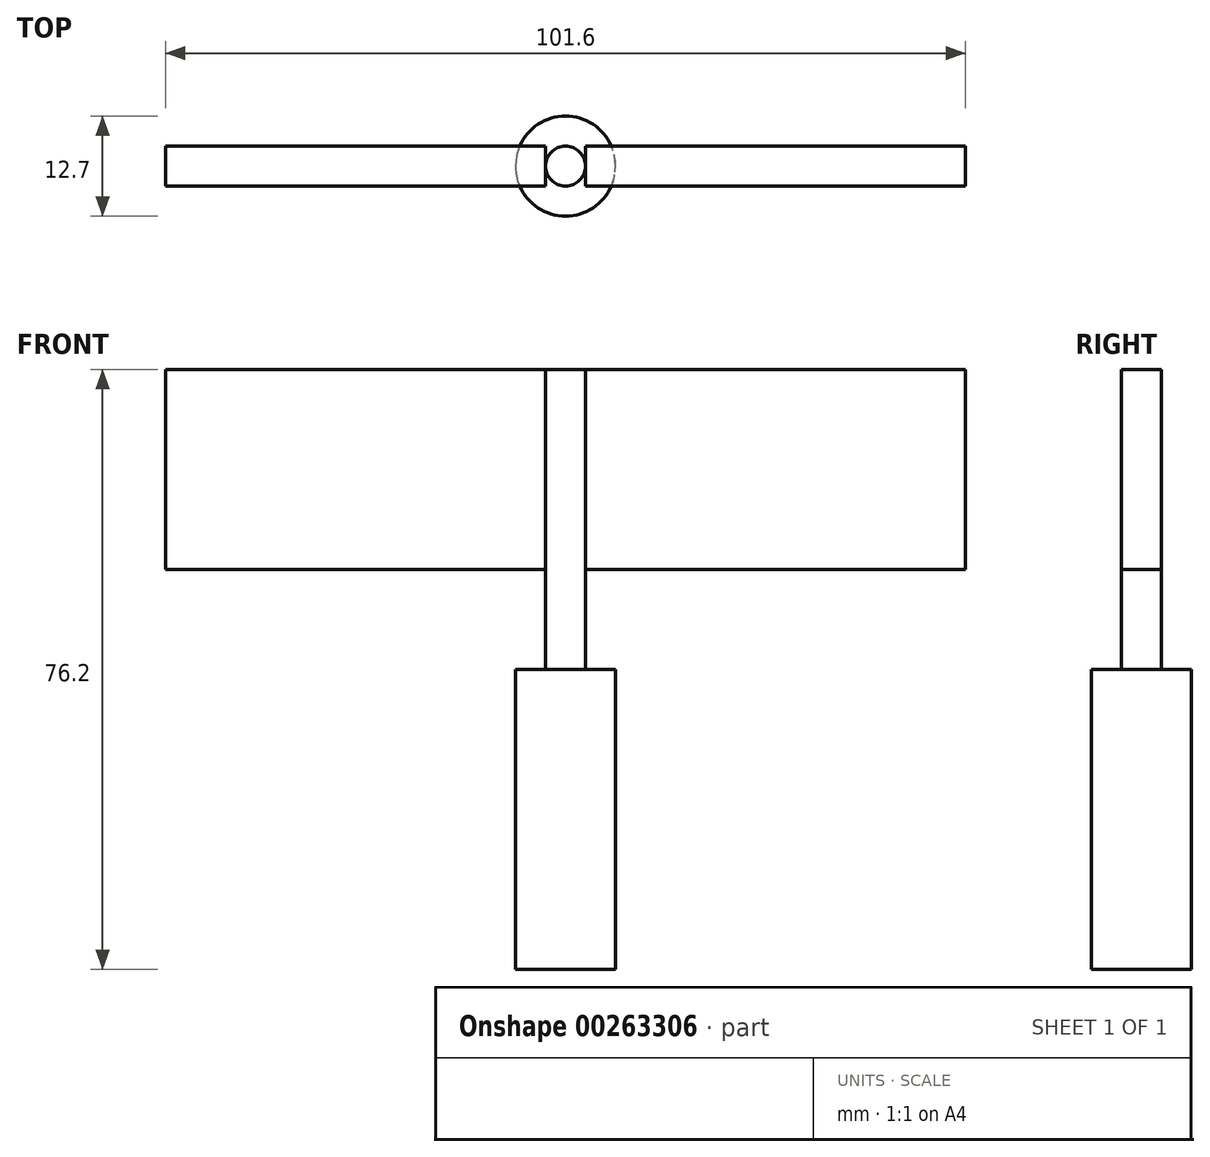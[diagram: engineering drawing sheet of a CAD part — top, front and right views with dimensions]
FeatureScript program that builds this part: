
annotation { "Feature Type Name" : "Feature", "Feature Type Description" : "" }
export const myFeature = defineFeature(function(context is Context, id is Id, definition is map)
    precondition{}
    {
        {
            var Q0;
            Q0=qCreatedBy(makeId("Front.planeOp"),FACE);
            var sketch = newSketch(context, id + "F0", { "sketchPlane" : qUnion([Q0])});
            skLineSegment(sketch, "E0", {"start": v(-126.4, 0) * mm, "end": v(-126.4, 12.7) * mm});
            skLineSegment(sketch, "E1", {"start": v(-126.4, 12.7) * mm, "end": v(-126.4, 63.5) * mm});
            skLineSegment(sketch, "E2.bottom", {"start": v(-177.2, 57.15) * mm, "end": v(-75.6, 57.15) * mm});
            skLineSegment(sketch, "E2.top", {"start": v(-177.2, 31.75) * mm, "end": v(-75.6, 31.75) * mm});
            skLineSegment(sketch, "E2.left", {"start": v(-177.2, 57.15) * mm, "end": v(-177.2, 31.75) * mm});
            skLineSegment(sketch, "E2.right", {"start": v(-75.6, 57.15) * mm, "end": v(-75.6, 31.75) * mm});
            skPoint(sketch, "E2.middle", {"position": v(-126.4, 44.45) * mm});
            skLineSegment(sketch, "E3.bottom", {"start": v(-132.76, 19.05) * mm, "end": v(-120.06, 19.05) * mm});
            skLineSegment(sketch, "E3.top", {"start": v(-132.76, -19.05) * mm, "end": v(-120.06, -19.05) * mm});
            skLineSegment(sketch, "E3.left", {"start": v(-132.76, 19.05) * mm, "end": v(-132.76, -19.05) * mm});
            skLineSegment(sketch, "E3.right", {"start": v(-120.06, 19.05) * mm, "end": v(-120.06, -19.05) * mm});
            skPoint(sketch, "E3.middle", {"position": v(-126.4, 0) * mm});
            skLineSegment(sketch, "E4.bottom", {"start": v(-128.95, 57.15) * mm, "end": v(-123.87, 57.15) * mm});
            skLineSegment(sketch, "E4.top", {"start": v(-128.95, 19.05) * mm, "end": v(-123.87, 19.05) * mm});
            skLineSegment(sketch, "E4.left", {"start": v(-128.95, 57.15) * mm, "end": v(-128.95, 19.05) * mm});
            skLineSegment(sketch, "E4.right", {"start": v(-123.87, 57.15) * mm, "end": v(-123.87, 19.05) * mm});
            skPoint(sketch, "E4.middle", {"position": v(-126.4, 38.1) * mm});
            skLineSegment(sketch, "E5", {"start": v(-126.4, 0) * mm, "end": v(-126.4, -19.05) * mm});
            skSolve(sketch);
        }
        {
            var Q0;
            {var subQ6=sQuery(id+"F0.wireOp",EDGE,"E0");Q0=makeQuery(id+"F0.imprint","IMPRINT",FACE,{"disambiguationData":[TD([[makeQuery(id+"F0.imprint","IMPRINT",EDGE,{"derivedFrom":subQ6}),1.0]])]});}
            var Q1;
            Q1=sQuery(id+"F0.wireOp",EDGE,"E0");
            revolve(context, id + "F1", {"entities" : qUnion([Q0]), "axis" : qUnion([Q1]), "revolveType" : RevolveType.FULL});
        }
        {
            var Q0;
            {var subQ3=sQuery(id+"F0.wireOp",EDGE,"E2.top");var subQ5=sQuery(id+"F0.wireOp",EDGE,"E4.left");var subQ6=makeQuery(id+"F0.imprint","INTERSECT",VERTEX,{"derivedFrom":[subQ3,subQ5]});Q0=makeQuery(id+"F0.imprint","IMPRINT",FACE,{"disambiguationData":[TD([[makeQuery(id+"F0.imprint","IMPRINT",EDGE,{"disambiguationData":[TD([[subQ6,-1.0]])],"derivedFrom":subQ3}),-1.0]])]});}
            var Q1;
            Q1=sQuery(id+"F0.wireOp",EDGE,"E1");
            revolve(context, id + "F2", {"operationType" : NewBodyOperationType.ADD, "entities" : qUnion([Q0]), "axis" : qUnion([Q1]), "revolveType" : RevolveType.FULL});
        }
        {
            var Q0;
            {var subQ0=sQuery(id+"F0.wireOp",EDGE,"E4.bottom");var subQ1=sQuery(id+"F0.wireOp",EDGE,"E1");var subQ2=makeQuery(id+"F0.imprint","INTERSECT",VERTEX,{"derivedFrom":[subQ1,subQ0]});Q0=makeQuery(id+"F0.imprint","IMPRINT",FACE,{"disambiguationData":[TD([[makeQuery(id+"F0.imprint","IMPRINT",EDGE,{"disambiguationData":[TD([[subQ2,1.0]])],"derivedFrom":subQ1}),1.0]])]});}
            var Q1;
            Q1=sQuery(id+"F0.wireOp",EDGE,"E1");
            revolve(context, id + "F3", {"operationType" : NewBodyOperationType.ADD, "entities" : qUnion([Q0]), "axis" : qUnion([Q1]), "revolveType" : RevolveType.FULL});
        }
        {
            var Q0;
            {var subQ0=sQuery(id+"F0.wireOp",EDGE,"E2.left");Q0=makeQuery(id+"F0.imprint","IMPRINT",FACE,{"disambiguationData":[TD([[makeQuery(id+"F0.imprint","IMPRINT",EDGE,{"derivedFrom":subQ0}),1.0]])]});}
            var Q1;
            {var subQ0=sQuery(id+"F0.wireOp",EDGE,"E2.right");Q1=makeQuery(id+"F0.imprint","IMPRINT",FACE,{"disambiguationData":[TD([[makeQuery(id+"F0.imprint","IMPRINT",EDGE,{"derivedFrom":subQ0}),-1.0]])]});}
            extrude(context, id + "F4", {"entities" : qUnion([Q0, Q1]), "endBound" : BoundingType.SYMMETRIC, "oppositeDirection" : true, "depth" : 5.08 * mm});
        }
    });
